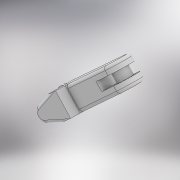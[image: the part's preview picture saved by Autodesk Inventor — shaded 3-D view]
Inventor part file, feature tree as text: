
AUTODESK INVENTOR PART (.ipt)
format: ipt  version: 2022 (Build 260153000, 153)  size: 238,080 bytes
history: native  units: mm
features: extrude x7, sketch x6, chamfer x2, fillet x2, plane x1, projected_geometry x1
ambient origin geometry x8: Origin, YZ Plane, XZ Plane, XY Plane, X Axis, Y Axis, Z Axis, Center Point
bodies: Solid1 (feature_tree)
feature tree (19):
  sketch  "Sketch1"  dims[d1=2.5mm d3=1.5mm]
  extrude  "Extrusion1"  Depth=2.5mm
  extrude  "Extrusion2"  Depth=7.0mm
  extrude  "Extrusion3"  Depth=35.0mm
  extrude  "Extrusion4"  Depth=10.0mm TaperAngle=0.0deg
  extrude  "Extrusion5"  Depth=18.0mm
  extrude  "Extrusion6"  Depth=0.5mm TaperAngle=0.0deg
  chamfer  "Chamfer1"  Distance=35.25mm
  fillet  "Fillet1"  Radius=7.0mm
  extrude  "Extrusion7"  Depth=0.5mm
  plane  "Work Plane1"
  fillet  "Fillet2"  Radius=1.2mm
  chamfer  "Chamfer2"  Distance=2.0mm Angle=45.0deg
  sketch  "Sketch2"  dims[d4=5.0mm d6=7.0mm]
  projected_geometry  "Projected Loop1"
  sketch  "Sketch3"  dims[d7=1.0mm d8=35.0mm]
  sketch  "Sketch4"  dims[d9=10.0mm d10=8.5mm d11=0.0mm]
  sketch  "Sketch5"  dims[d12=12.5mm d13=0.0mm d14=18.0mm]
  sketch  "Sketch6"  dims[d15=2.5mm d16=12.5mm d17=0.0mm d18=35.25mm d19=0.0mm d20=7.0mm d21=0.0mm d22=8.1mm d23=1.2mm d24=0.0mm d25=2.0mm d26=2.0mm d27=45.0deg d28=1.0mm d29=5.0mm d30=1.2mm d31=0.0mm d32=0.5mm d33=1.0mm d34=2.0mm d35=45.0deg]
